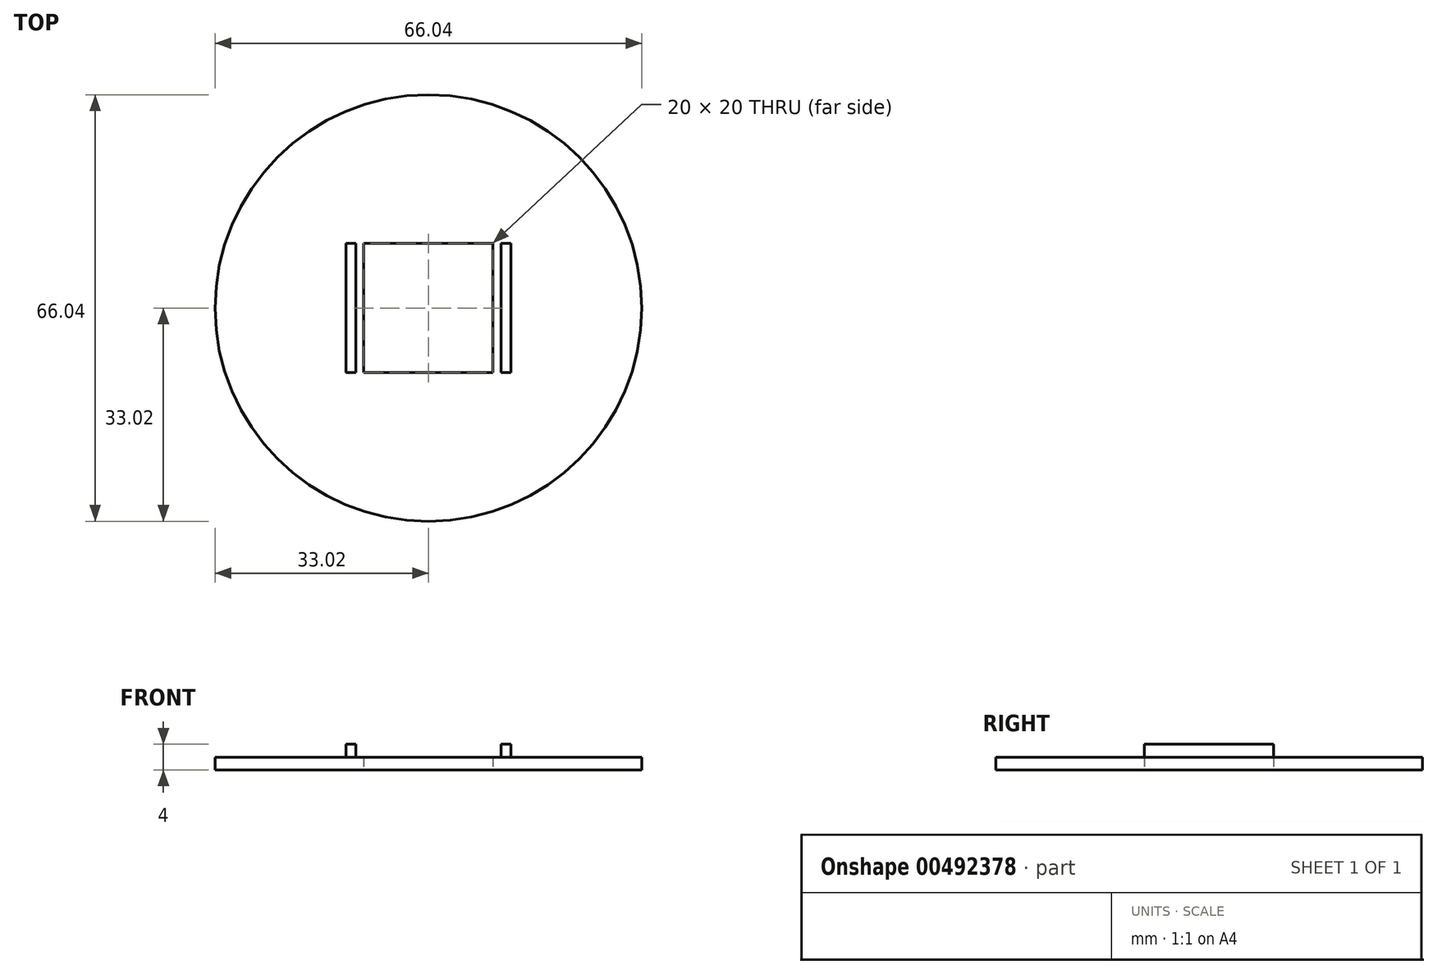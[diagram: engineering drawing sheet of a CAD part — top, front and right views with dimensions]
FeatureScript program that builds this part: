
annotation { "Feature Type Name" : "Feature", "Feature Type Description" : "" }
export const myFeature = defineFeature(function(context is Context, id is Id, definition is map)
    precondition{}
    {
        {
            var Q0;
            Q0=qCreatedBy(makeId("Top.planeOp"),FACE);
            var sketch = newSketch(context, id + "F0", { "sketchPlane" : qUnion([Q0])});
            skCircle(sketch, "E0", {"center": v(0, 0) * mm, "radius": 33.02 * mm});
            skLineSegment(sketch, "E1.bottom", {"start": v(-10, -10) * mm, "end": v(10, -10) * mm});
            skLineSegment(sketch, "E1.top", {"start": v(-10, 10) * mm, "end": v(10, 10) * mm});
            skLineSegment(sketch, "E1.left", {"start": v(-10, -10) * mm, "end": v(-10, 10) * mm});
            skLineSegment(sketch, "E1.right", {"start": v(10, -10) * mm, "end": v(10, 10) * mm});
            skLineSegment(sketch, "E2.bottom", {"start": v(14.78, 10) * mm, "end": v(13.28, 10) * mm});
            skLineSegment(sketch, "E2.top", {"start": v(14.78, -10) * mm, "end": v(13.28, -10) * mm});
            skLineSegment(sketch, "E2.left", {"start": v(14.78, 10) * mm, "end": v(14.78, -10) * mm});
            skLineSegment(sketch, "E2.right", {"start": v(13.28, 10) * mm, "end": v(13.28, -10) * mm});
            skLineSegment(sketch, "E3", {"start": v(0, 10) * mm, "end": v(0, -10) * mm});
            skLineSegment(sketch, "E4.MirrorCS", {"start": v(-13.28, 10) * mm, "end": v(-13.28, -10) * mm});
            skLineSegment(sketch, "E5.MirrorCS", {"start": v(-14.78, 10) * mm, "end": v(-13.28, 10) * mm});
            skLineSegment(sketch, "E6.MirrorCS", {"start": v(-14.78, 10) * mm, "end": v(-14.78, -10) * mm});
            skLineSegment(sketch, "E7.MirrorCS", {"start": v(-14.78, -10) * mm, "end": v(-13.28, -10) * mm});
            skSolve(sketch);
        }
        {
            var Q0;
            Q0=makeQuery(id+"F0.imprint","IMPRINT",FACE,{"disambiguationData":[TD([[makeQuery(id+"F0.imprint","IMPRINT",EDGE,{"derivedFrom":sQuery(id+"F0.wireOp",EDGE,"E0")}),1.0]])]});
            var Q1;
            Q1=makeQuery(id+"F0.imprint","IMPRINT",FACE,{"disambiguationData":[TD([[makeQuery(id+"F0.imprint","IMPRINT",EDGE,{"derivedFrom":sQuery(id+"F0.wireOp",EDGE,"E4.MirrorCS")}),-1.0]])]});
            var Q2;
            Q2=makeQuery(id+"F0.imprint","IMPRINT",FACE,{"disambiguationData":[TD([[makeQuery(id+"F0.imprint","IMPRINT",EDGE,{"derivedFrom":sQuery(id+"F0.wireOp",EDGE,"E2.bottom")}),1.0]])]});
            extrude(context, id + "F1", {"entities" : qUnion([Q0, Q1, Q2]), "depth" : 2 * mm});
        }
        {
            var Q0;
            Q0=makeQuery(id+"F1.opExtrude","CAP_FACE",FACE,{"disambiguationData":[OSD([sQuery(id+"F0.wireOp",EDGE,"E0"),sQuery(id+"F0.wireOp",EDGE,"E1.bottom"),sQuery(id+"F0.wireOp",EDGE,"E1.top"),sQuery(id+"F0.wireOp",EDGE,"E1.left"),sQuery(id+"F0.wireOp",EDGE,"E1.right")])],"isStart":false});
            var sketch = newSketch(context, id + "F2", { "sketchPlane" : qUnion([Q0])});
            skLineSegment(sketch, "E8.bottom", {"start": v(-11.25, 10) * mm, "end": v(-12.75, 10) * mm});
            skLineSegment(sketch, "E8.top", {"start": v(-11.25, -10) * mm, "end": v(-12.75, -10) * mm});
            skLineSegment(sketch, "E8.left", {"start": v(-11.25, 10) * mm, "end": v(-11.25, -10) * mm});
            skLineSegment(sketch, "E8.right", {"start": v(-12.75, 10) * mm, "end": v(-12.75, -10) * mm});
            skLineSegment(sketch, "E9", {"start": v(0, 13.96) * mm, "end": v(0, -13.9) * mm});
            skPoint(sketch, "E9.endSnap0", {"position": v(0, -10) * mm});
            skLineSegment(sketch, "E10.MirrorCS", {"start": v(11.25, 10) * mm, "end": v(11.25, -10) * mm});
            skLineSegment(sketch, "E11.MirrorCS", {"start": v(12.75, 10) * mm, "end": v(12.75, -10) * mm});
            skLineSegment(sketch, "E12.MirrorCS", {"start": v(11.25, 10) * mm, "end": v(12.75, 10) * mm});
            skLineSegment(sketch, "E13.MirrorCS", {"start": v(11.25, -10) * mm, "end": v(12.75, -10) * mm});
            skSolve(sketch);
        }
        {
            var Q0;
            Q0=makeQuery(id+"F2.imprint","IMPRINT",FACE,{"disambiguationData":[TD([[makeQuery(id+"F2.imprint","IMPRINT",EDGE,{"derivedFrom":sQuery(id+"F2.wireOp",EDGE,"E8.bottom")}),1.0]])]});
            var Q1;
            Q1=makeQuery(id+"F2.imprint","IMPRINT",FACE,{"disambiguationData":[TD([[makeQuery(id+"F2.imprint","IMPRINT",EDGE,{"derivedFrom":sQuery(id+"F2.wireOp",EDGE,"E10.MirrorCS")}),1.0]])]});
            extrude(context, id + "F3", {"entities" : qUnion([Q0, Q1]), "operationType" : NewBodyOperationType.ADD, "depth" : 2 * mm});
        }
    });
